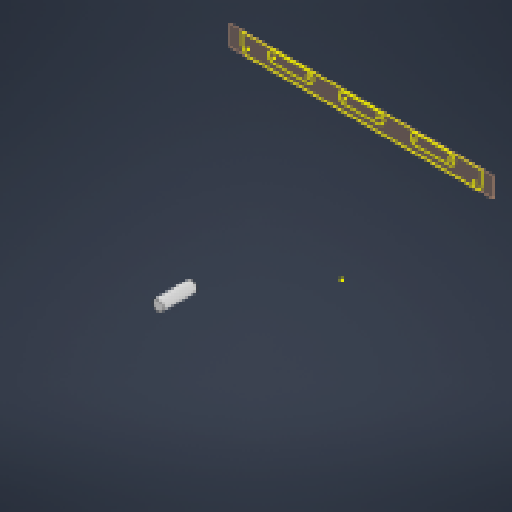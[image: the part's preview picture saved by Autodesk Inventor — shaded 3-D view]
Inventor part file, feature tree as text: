
AUTODESK INVENTOR PART (.ipt)
format: ipt  version: 2025 (Build 290162000, 162)  size: 122,368 bytes
history: native  units: mm
features: reference x5, other x3, sketch x2, plane x1
ambient origin geometry x8: Origin, YZ Plane, XZ Plane, XY Plane, X Axis, Y Axis, Z Axis, Center Point
feature tree (11):
  sketch  "Sketch1"
  plane  "Work Plane1"
  sketch  "Sketch2"
  reference  "Reference1"
  reference  "Reference2"
  reference  "Reference3"
  reference  "Reference4"
  reference  "Reference5"
  other  "hotend-new.iam"
  other  "rails-bolts:1"
  other  "hemera-xs-duct-mount-v2-eddy:1"
